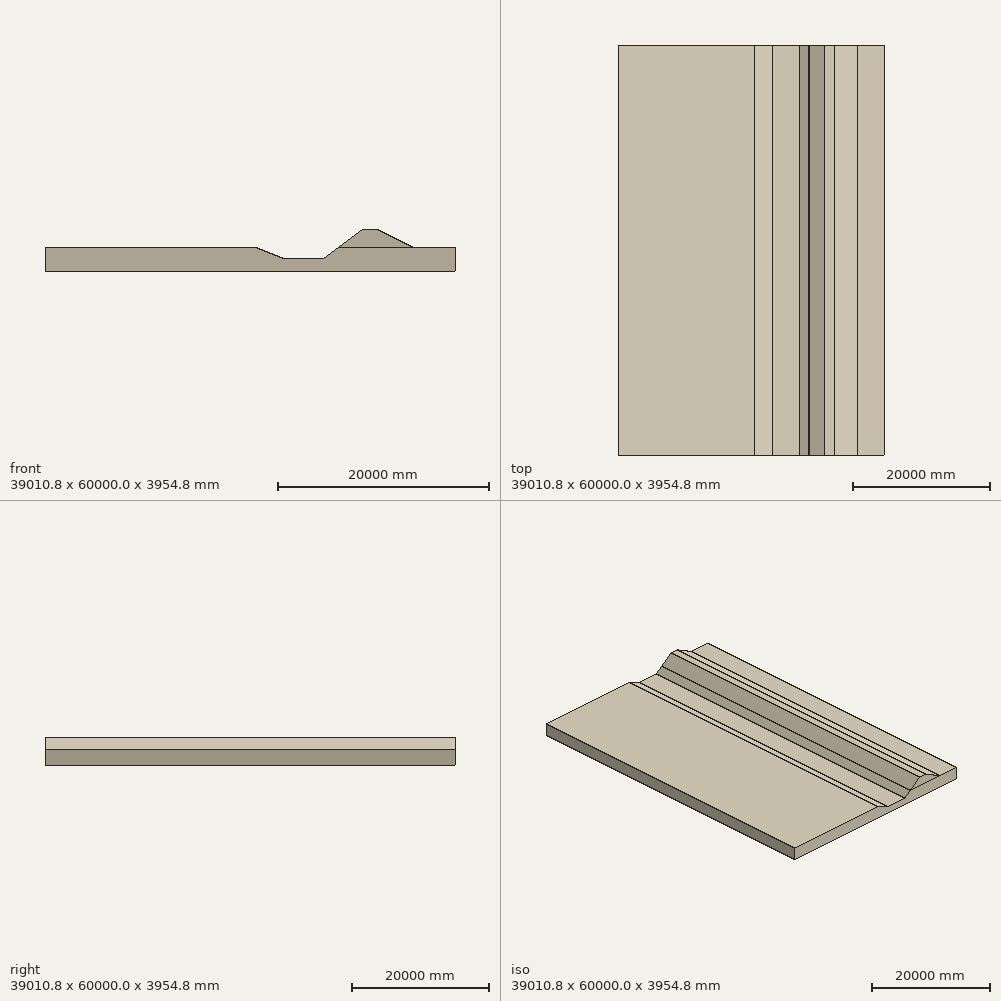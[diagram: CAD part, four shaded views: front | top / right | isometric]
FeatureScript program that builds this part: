
annotation { "Feature Type Name" : "Feature", "Feature Type Description" : "" }
export const myFeature = defineFeature(function(context is Context, id is Id, definition is map)
    precondition{}
    {
        {
            var Q0;
            Q0=qCreatedBy(makeId("Front.planeOp"),FACE);
            var sketch = newSketch(context, id + "F0", { "sketchPlane" : qUnion([Q0])});
            skLineSegment(sketch, "E0", {"start": v(0, 0) * mm, "end": v(2236.45, 1677.34) * mm});
            skLineSegment(sketch, "E1", {"start": v(2236.45, 1677.34) * mm, "end": v(3736.45, 1677.34) * mm});
            skLineSegment(sketch, "E2", {"start": v(3736.45, 1677.34) * mm, "end": v(7090.4, 0) * mm});
            skLineSegment(sketch, "E3", {"start": v(7090.4, 0) * mm, "end": v(11090.4, 0) * mm});
            skLineSegment(sketch, "E4", {"start": v(2236.45, 1677.34) * mm, "end": v(2236.45, 0) * mm});
            skLineSegment(sketch, "E5", {"start": v(2236.45, 0) * mm, "end": v(0, 0) * mm});
            skLineSegment(sketch, "E6", {"start": v(3736.45, 1677.34) * mm, "end": v(3736.45, 0) * mm});
            skLineSegment(sketch, "E7", {"start": v(3736.45, 0) * mm, "end": v(7090.4, 0) * mm});
            skLineSegment(sketch, "E8", {"start": v(2236.45, 0) * mm, "end": v(3736.45, 0) * mm});
            skLineSegment(sketch, "E9", {"start": v(0, 0) * mm, "end": v(-1363.55, -1022.67) * mm});
            skLineSegment(sketch, "E10", {"start": v(-1363.55, -1022.67) * mm, "end": v(-5363.55, -1022.67) * mm});
            skLineSegment(sketch, "E11", {"start": v(-5363.55, -1022.67) * mm, "end": v(-7920.4, 0) * mm});
            skLineSegment(sketch, "E12", {"start": v(-7920.4, 0) * mm, "end": v(-7920.4, -1022.67) * mm});
            skLineSegment(sketch, "E13", {"start": v(-7920.4, -1022.67) * mm, "end": v(-5363.55, -1022.67) * mm});
            skLineSegment(sketch, "E14", {"start": v(-7920.4, 0) * mm, "end": v(-27920.4, 0) * mm});
            skLineSegment(sketch, "E15", {"start": v(0, 0) * mm, "end": v(-7920.4, 0) * mm});
            skLineSegment(sketch, "E16", {"start": v(-1363.55, -1022.67) * mm, "end": v(11090.4, -1022.67) * mm});
            skLineSegment(sketch, "E17", {"start": v(-7920.4, -1022.67) * mm, "end": v(-27920.4, -1022.67) * mm});
            skLineSegment(sketch, "E18", {"start": v(-27920.4, -1022.67) * mm, "end": v(-27920.4, 0) * mm});
            skLineSegment(sketch, "E19", {"start": v(11090.4, -1022.67) * mm, "end": v(11090.4, 0) * mm});
            skLineSegment(sketch, "E20", {"start": v(2236.45, 0) * mm, "end": v(2236.45, -1022.67) * mm});
            skLineSegment(sketch, "E21", {"start": v(0, 0) * mm, "end": v(0, -1022.67) * mm});
            skLineSegment(sketch, "E22", {"start": v(-27920.4, -1022.67) * mm, "end": v(-27920.4, -2277.44) * mm});
            skLineSegment(sketch, "E23", {"start": v(-27920.4, -2277.44) * mm, "end": v(11090.4, -2277.44) * mm});
            skLineSegment(sketch, "E24", {"start": v(11090.4, -2277.44) * mm, "end": v(11090.4, -1022.67) * mm});
            skSolve(sketch);
        }
        {
            var Q0;
            Q0=makeQuery(id+"F0.imprint","IMPRINT",FACE,{"disambiguationData":[TD([[makeQuery(id+"F0.imprint","IMPRINT",EDGE,{"derivedFrom":sQuery(id+"F0.wireOp",EDGE,"E1")}),-1.0]])]});
            var Q1;
            Q1=makeQuery(id+"F0.imprint","IMPRINT",FACE,{"disambiguationData":[TD([[makeQuery(id+"F0.imprint","IMPRINT",EDGE,{"derivedFrom":sQuery(id+"F0.wireOp",EDGE,"E0")}),-1.0]])]});
            var Q2;
            Q2=makeQuery(id+"F0.imprint","IMPRINT",FACE,{"disambiguationData":[TD([[makeQuery(id+"F0.imprint","IMPRINT",EDGE,{"derivedFrom":sQuery(id+"F0.wireOp",EDGE,"E2")}),-1.0]])]});
            extrude(context, id + "F1", {"entities" : qUnion([Q0, Q1, Q2]), "oppositeDirection" : true, "depth" : 60000 * mm, "offsetDistance" : 25 * mm});
        }
        {
            var Q0;
            Q0=makeQuery(id+"F0.imprint","IMPRINT",FACE,{"disambiguationData":[TD([[makeQuery(id+"F0.imprint","IMPRINT",EDGE,{"derivedFrom":sQuery(id+"F0.wireOp",EDGE,"E12")}),-1.0]])]});
            var Q1;
            Q1=makeQuery(id+"F0.imprint","IMPRINT",FACE,{"disambiguationData":[TD([[makeQuery(id+"F0.imprint","IMPRINT",EDGE,{"derivedFrom":sQuery(id+"F0.wireOp",EDGE,"E11")}),1.0]])]});
            var Q2;
            {var subQ0=sQuery(id+"F0.wireOp",EDGE,"E9");Q2=makeQuery(id+"F0.imprint","IMPRINT",FACE,{"disambiguationData":[TD([[makeQuery(id+"F0.imprint","IMPRINT",EDGE,{"derivedFrom":subQ0}),1.0]])]});}
            var Q3;
            Q3=makeQuery(id+"F0.imprint","IMPRINT",FACE,{"disambiguationData":[TD([[makeQuery(id+"F0.imprint","IMPRINT",EDGE,{"derivedFrom":sQuery(id+"F0.wireOp",EDGE,"E5")}),1.0]])]});
            var Q4;
            Q4=makeQuery(id+"F0.imprint","IMPRINT",FACE,{"disambiguationData":[TD([[makeQuery(id+"F0.imprint","IMPRINT",EDGE,{"derivedFrom":sQuery(id+"F0.wireOp",EDGE,"E3")}),-1.0]])]});
            var Q5;
            {var subQ3=sQuery(id+"F0.wireOp",EDGE,"E10");Q5=makeQuery(id+"F0.imprint","IMPRINT",FACE,{"disambiguationData":[TD([[makeQuery(id+"F0.imprint","IMPRINT",EDGE,{"derivedFrom":subQ3}),1.0]])]});}
            extrude(context, id + "F2", {"entities" : qUnion([Q0, Q1, Q2, Q3, Q4, Q5]), "oppositeDirection" : true, "depth" : 60000 * mm, "offsetDistance" : 25 * mm});
        }
    });
